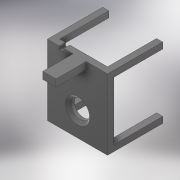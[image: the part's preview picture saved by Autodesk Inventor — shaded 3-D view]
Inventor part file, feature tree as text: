
AUTODESK INVENTOR PART (.ipt)
format: ipt  version: 2020 (Build 240168000, 168)  size: 218,624 bytes
history: native  units: mm
features: extrude x6, sketch x6, chamfer x1
ambient origin geometry x8: Origin, YZ Plane, XZ Plane, XY Plane, X Axis, Y Axis, Z Axis, Center Point
bodies: Volumenkörper1 (feature_tree)
feature tree (13):
  extrude  "Extrusion1"  Depth=98.0mm
  extrude  "Extrusion2"  Depth=21.5mm
  extrude  "Extrusion3"  Depth=34.85mm
  extrude  "Extrusion4"  Depth=4.0mm
  extrude  "Extrusion5"  Depth=4.0mm
  extrude  "Extrusion6"  Depth=1.5mm
  chamfer  "Fase1"  Distance=1.5mm
  sketch  "Skizze1"  dims[d0=115.0mm d1=98.0mm]
  sketch  "Skizze2"  dims[d2=10.0mm d3=0.0mm d4=21.5mm]
  sketch  "Skizze3"  dims[d5=11.5mm d6=34.85mm]
  sketch  "Skizze4"  dims[d7=49.2mm d8=0.0mm d9=4.0mm]
  sketch  "Skizze5"  dims[d10=4.0mm d11=4.0mm]
  sketch  "Skizze6"  dims[d12=4.0mm d13=1.5mm d14=1.5mm d15=17.5mm d16=0.0mm d17=7.0mm d18=5.0mm d19=15.0mm d20=10.0mm d21=0.0mm d22=10.0mm d23=10.0mm d24=10.0mm d25=10.0mm d26=10.0mm d27=10.0mm d28=10.0mm d29=10.0mm d30=80.0mm d31=0.0mm d32=30.0mm d33=49.0mm d34=65.0mm d35=10.0mm d36=0.0mm d37=5.0mm d38=2.0mm d39=45.0deg d40=0.0mm]
